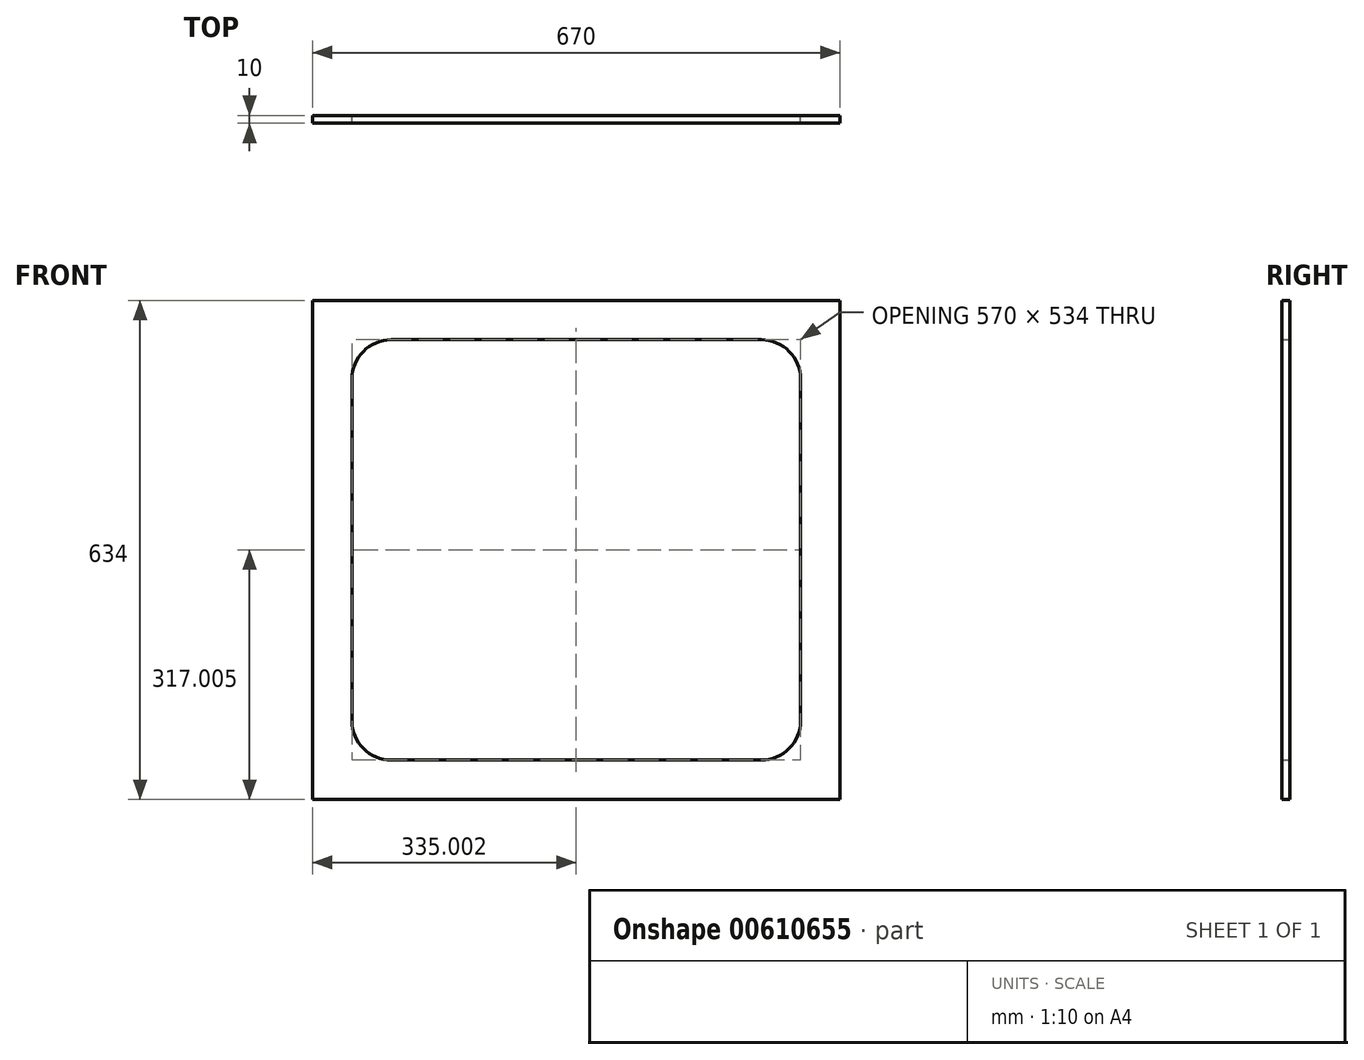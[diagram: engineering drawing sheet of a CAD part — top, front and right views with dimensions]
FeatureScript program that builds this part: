
annotation { "Feature Type Name" : "Feature", "Feature Type Description" : "" }
export const myFeature = defineFeature(function(context is Context, id is Id, definition is map)
    precondition{}
    {
        {
            var Q0;
            Q0=qCreatedBy(makeId("Front.planeOp"),FACE);
            var sketch = newSketch(context, id + "F0", { "sketchPlane" : qUnion([Q0])});
            skLineSegment(sketch, "E0.top", {"start": v(-341.35, -229.92) * mm, "end": v(328.65, -229.92) * mm});
            skLineSegment(sketch, "E1", {"start": v(-341.35, 404.08) * mm, "end": v(328.65, 404.08) * mm});
            skLineSegment(sketch, "E2", {"start": v(-341.35, 404.08) * mm, "end": v(-341.35, -229.92) * mm});
            skLineSegment(sketch, "E3", {"start": v(328.65, 404.08) * mm, "end": v(328.65, -229.92) * mm});
            skLineSegment(sketch, "E4", {"start": v(-241.35, 354.08) * mm, "end": v(228.65, 354.08) * mm});
            skLineSegment(sketch, "E5", {"start": v(-291.35, 304.08) * mm, "end": v(-291.35, -129.92) * mm});
            skLineSegment(sketch, "E6", {"start": v(-241.35, -179.92) * mm, "end": v(228.65, -179.92) * mm});
            skLineSegment(sketch, "E7", {"start": v(278.65, -129.92) * mm, "end": v(278.65, 304.08) * mm});
            skPoint(sketch, "E8.visualSharp", {"position": v(-291.35, 354.08) * mm});
            skArc(sketch, "E8.filletArc", {"start": v(-241.35, 354.08) * mm, "mid": v(-276.7, 339.44) * mm, "end": v(-291.35, 304.08) * mm});
            skPoint(sketch, "E9.visualSharp", {"position": v(278.65, 354.08) * mm});
            skArc(sketch, "E9.filletArc", {"start": v(278.65, 304.08) * mm, "mid": v(264, 339.44) * mm, "end": v(228.65, 354.08) * mm});
            skPoint(sketch, "E10.visualSharp", {"position": v(278.65, -179.92) * mm});
            skArc(sketch, "E10.filletArc", {"start": v(228.65, -179.92) * mm, "mid": v(264, -165.27) * mm, "end": v(278.65, -129.92) * mm});
            skPoint(sketch, "E11.visualSharp", {"position": v(-291.35, -179.92) * mm});
            skArc(sketch, "E11.filletArc", {"start": v(-291.35, -129.92) * mm, "mid": v(-276.7, -165.27) * mm, "end": v(-241.35, -179.92) * mm});
            skSolve(sketch);
        }
        {
            var Q0;
            Q0=makeQuery(id+"F0.imprint","IMPRINT",FACE,{"disambiguationData":[TD([[makeQuery(id+"F0.imprint","IMPRINT",EDGE,{"derivedFrom":sQuery(id+"F0.wireOp",EDGE,"E0.bottom")}),-1.0]])]});
            var Q1;
            Q1=makeQuery(id+"F0.imprint","IMPRINT",FACE,{"disambiguationData":[TD([[makeQuery(id+"F0.imprint","IMPRINT",EDGE,{"derivedFrom":sQuery(id+"F0.wireOp",EDGE,"E0.top")}),1.0]])]});
            extrude(context, id + "F1", {"entities" : qUnion([Q0, Q1]), "depth" : 10 * mm, "offsetDistance" : 25 * mm});
        }
    });
